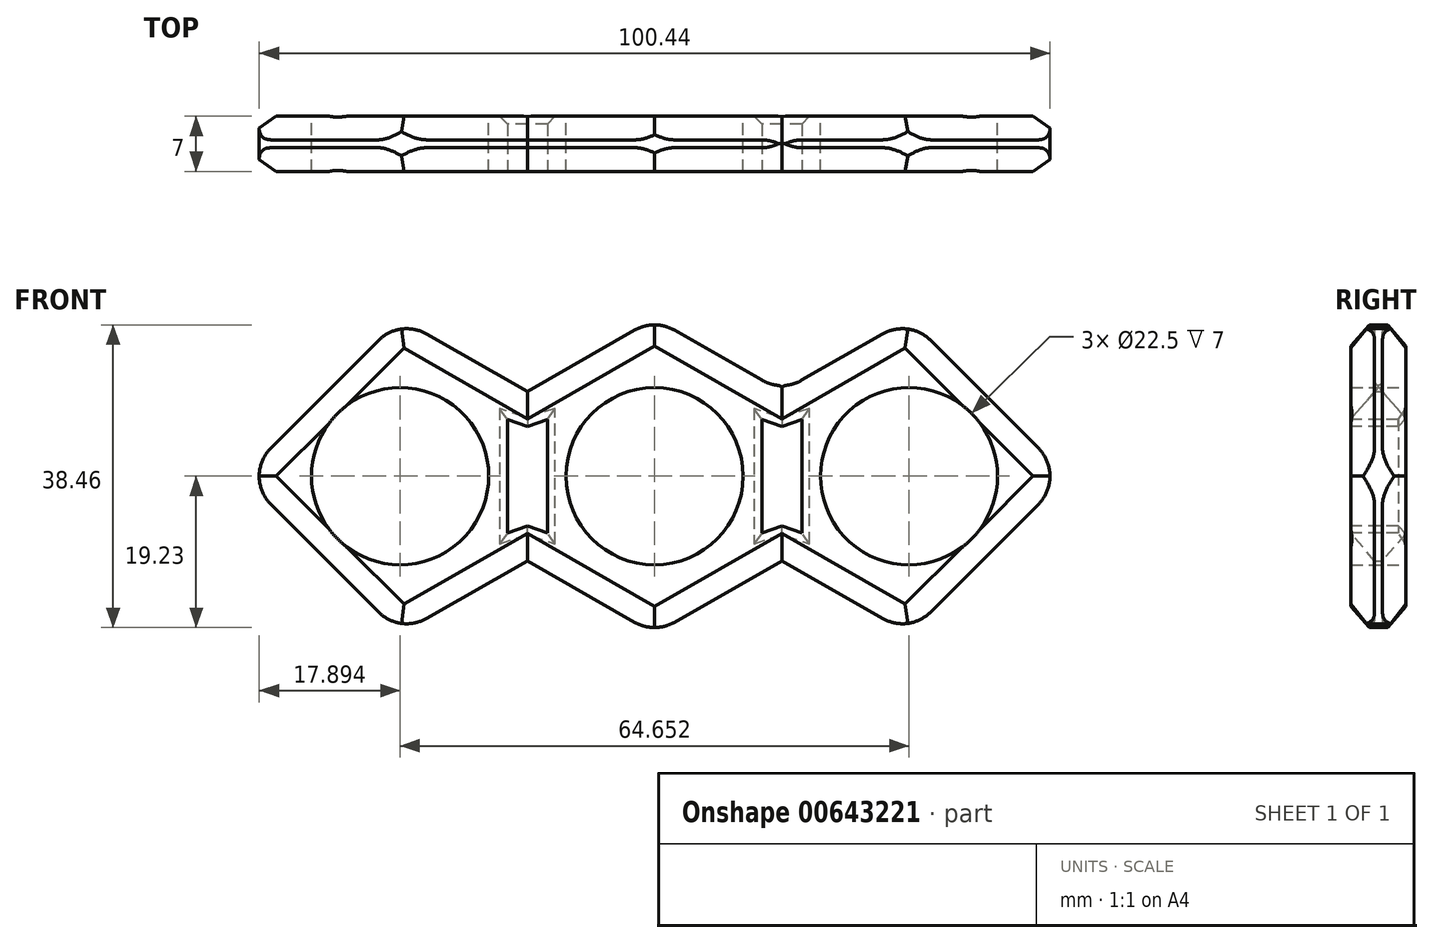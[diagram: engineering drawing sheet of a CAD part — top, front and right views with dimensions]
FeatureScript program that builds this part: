
annotation { "Feature Type Name" : "Feature", "Feature Type Description" : "" }
export const myFeature = defineFeature(function(context is Context, id is Id, definition is map)
    precondition{}
    {
        {
            var Q0;
            Q0=qCreatedBy(makeId("Front.planeOp"),FACE);
            var sketch = newSketch(context, id + "F0", { "sketchPlane" : qUnion([Q0])});
            skCircle(sketch, "E0", {"center": v(0, 0) * mm, "radius": 11.25 * mm});
            skLineSegment(sketch, "E1", {"start": v(0, 0) * mm, "end": v(-32.33, 0) * mm});
            skLineSegment(sketch, "E2.MirrorCS", {"start": v(0, 0) * mm, "end": v(32.33, 0) * mm});
            skCircle(sketch, "E3", {"center": v(-32.33, 0) * mm, "radius": 11.25 * mm});
            skCircle(sketch, "E4", {"center": v(32.33, 0) * mm, "radius": 11.25 * mm});
            skLineSegment(sketch, "E5", {"start": v(-32.33, 0) * mm, "end": v(-52.33, 0) * mm});
            skLineSegment(sketch, "E6.MirrorCS", {"start": v(32.33, 0) * mm, "end": v(52.33, 0) * mm});
            skLineSegment(sketch, "E7", {"start": v(-32.33, 0) * mm, "end": v(-32.33, 20) * mm});
            skLineSegment(sketch, "E8", {"start": v(-32.33, 0) * mm, "end": v(-32.33, -20) * mm});
            skLineSegment(sketch, "E9", {"start": v(-52.33, 0) * mm, "end": v(-32.33, -20) * mm});
            skLineSegment(sketch, "E10", {"start": v(-52.33, 0) * mm, "end": v(-32.33, 20) * mm});
            skLineSegment(sketch, "E11", {"start": v(-16.16, 0) * mm, "end": v(-16.16, 10.75) * mm});
            skLineSegment(sketch, "E12", {"start": v(-16.16, 10.75) * mm, "end": v(-32.33, 20) * mm});
            skLineSegment(sketch, "E13.MirrorCS", {"start": v(-16.16, -10.75) * mm, "end": v(-32.33, -20) * mm});
            skLineSegment(sketch, "E14.MirrorCS", {"start": v(-16.16, 0) * mm, "end": v(-16.16, -10.75) * mm});
            skLineSegment(sketch, "E15", {"start": v(0, 0) * mm, "end": v(0, 20) * mm});
            skLineSegment(sketch, "E16", {"start": v(0, 0) * mm, "end": v(0, -20) * mm});
            skLineSegment(sketch, "E17", {"start": v(-16.16, 10.75) * mm, "end": v(0, 20) * mm});
            skLineSegment(sketch, "E18", {"start": v(-16.16, -10.75) * mm, "end": v(0, -20) * mm});
            skLineSegment(sketch, "E19.MirrorCS", {"start": v(16.16, 10.75) * mm, "end": v(0, 20) * mm});
            skLineSegment(sketch, "E20.MirrorCS", {"start": v(16.16, -10.75) * mm, "end": v(0, -20) * mm});
            skLineSegment(sketch, "E21.MirrorCS", {"start": v(52.33, 0) * mm, "end": v(32.33, -20) * mm});
            skLineSegment(sketch, "E22.MirrorCS", {"start": v(52.33, 0) * mm, "end": v(32.33, 20) * mm});
            skLineSegment(sketch, "E23.MirrorCS", {"start": v(16.16, 10.75) * mm, "end": v(32.33, 20) * mm});
            skLineSegment(sketch, "E24.MirrorCS", {"start": v(16.16, -10.75) * mm, "end": v(32.33, -20) * mm});
            skLineSegment(sketch, "E25.MirrorCS", {"start": v(16.16, 0) * mm, "end": v(16.16, 10.75) * mm});
            skLineSegment(sketch, "E26.MirrorCS", {"start": v(16.16, 0) * mm, "end": v(16.16, -10.75) * mm});
            skSolve(sketch);
        }
        {
            var Q0;
            {var subQ0=sQuery(id+"F0.wireOp",EDGE,"E22.MirrorCS");Q0=makeQuery(id+"F0.imprint","IMPRINT",FACE,{"disambiguationData":[TD([[makeQuery(id+"F0.imprint","IMPRINT",EDGE,{"derivedFrom":subQ0}),1.0]])]});}
            var Q1;
            {var subQ0=sQuery(id+"F0.wireOp",EDGE,"E21.MirrorCS");Q1=makeQuery(id+"F0.imprint","IMPRINT",FACE,{"disambiguationData":[TD([[makeQuery(id+"F0.imprint","IMPRINT",EDGE,{"derivedFrom":subQ0}),-1.0]])]});}
            var Q2;
            {var subQ0=sQuery(id+"F0.wireOp",EDGE,"E20.MirrorCS");Q2=makeQuery(id+"F0.imprint","IMPRINT",FACE,{"disambiguationData":[TD([[makeQuery(id+"F0.imprint","IMPRINT",EDGE,{"derivedFrom":subQ0}),-1.0]])]});}
            var Q3;
            {var subQ0=sQuery(id+"F0.wireOp",EDGE,"E19.MirrorCS");Q3=makeQuery(id+"F0.imprint","IMPRINT",FACE,{"disambiguationData":[TD([[makeQuery(id+"F0.imprint","IMPRINT",EDGE,{"derivedFrom":subQ0}),1.0]])]});}
            var Q4;
            {var subQ4=sQuery(id+"F0.wireOp",EDGE,"E11");Q4=makeQuery(id+"F0.imprint","IMPRINT",FACE,{"disambiguationData":[TD([[makeQuery(id+"F0.imprint","IMPRINT",EDGE,{"derivedFrom":subQ4}),-1.0]])]});}
            var Q5;
            {var subQ0=sQuery(id+"F0.wireOp",EDGE,"E14.MirrorCS");Q5=makeQuery(id+"F0.imprint","IMPRINT",FACE,{"disambiguationData":[TD([[makeQuery(id+"F0.imprint","IMPRINT",EDGE,{"derivedFrom":subQ0}),1.0]])]});}
            var Q6;
            {var subQ0=sQuery(id+"F0.wireOp",EDGE,"E13.MirrorCS");Q6=makeQuery(id+"F0.imprint","IMPRINT",FACE,{"disambiguationData":[TD([[makeQuery(id+"F0.imprint","IMPRINT",EDGE,{"derivedFrom":subQ0}),-1.0]])]});}
            var Q7;
            {var subQ5=sQuery(id+"F0.wireOp",EDGE,"E9");Q7=makeQuery(id+"F0.imprint","IMPRINT",FACE,{"disambiguationData":[TD([[makeQuery(id+"F0.imprint","IMPRINT",EDGE,{"derivedFrom":subQ5}),1.0]])]});}
            var Q8;
            {var subQ5=sQuery(id+"F0.wireOp",EDGE,"E10");Q8=makeQuery(id+"F0.imprint","IMPRINT",FACE,{"disambiguationData":[TD([[makeQuery(id+"F0.imprint","IMPRINT",EDGE,{"derivedFrom":subQ5}),-1.0]])]});}
            var Q9;
            {var subQ0=sQuery(id+"F0.wireOp",EDGE,"E11");Q9=makeQuery(id+"F0.imprint","IMPRINT",FACE,{"disambiguationData":[TD([[makeQuery(id+"F0.imprint","IMPRINT",EDGE,{"derivedFrom":subQ0}),1.0]])]});}
            extrude(context, id + "F1", {"entities" : qUnion([Q0, Q1, Q2, Q3, Q4, Q5, Q6, Q7, Q8, Q9]), "depth" : 7 * mm, "offsetDistance" : 25.4 * mm});
        }
        {
            var Q0;
            Q0=makeQuery(id+"F1.opExtrude","CAP_FACE",FACE,{"disambiguationData":[OSD([sQuery(id+"F0.wireOp",EDGE,"E0"),sQuery(id+"F0.wireOp",EDGE,"E3"),sQuery(id+"F0.wireOp",EDGE,"E4"),sQuery(id+"F0.wireOp",EDGE,"E9"),sQuery(id+"F0.wireOp",EDGE,"E10"),sQuery(id+"F0.wireOp",EDGE,"E12"),sQuery(id+"F0.wireOp",EDGE,"E13.MirrorCS"),sQuery(id+"F0.wireOp",EDGE,"E17"),sQuery(id+"F0.wireOp",EDGE,"E18"),sQuery(id+"F0.wireOp",EDGE,"E19.MirrorCS"),sQuery(id+"F0.wireOp",EDGE,"E20.MirrorCS"),sQuery(id+"F0.wireOp",EDGE,"E21.MirrorCS"),sQuery(id+"F0.wireOp",EDGE,"E22.MirrorCS"),sQuery(id+"F0.wireOp",EDGE,"E23.MirrorCS"),sQuery(id+"F0.wireOp",EDGE,"E24.MirrorCS")])],"isStart":false});
            var sketch = newSketch(context, id + "F2", { "sketchPlane" : qUnion([Q0])});
            skLineSegment(sketch, "E27", {"start": v(16.16, -8.44) * mm, "end": v(16.16, 8.44) * mm});
            skLineSegment(sketch, "E28", {"start": v(-16.16, -8.44) * mm, "end": v(-16.16, 8.44) * mm});
            skLineSegment(sketch, "E29", {"start": v(13.63, -9.9) * mm, "end": v(13.63, 9.9) * mm});
            skLineSegment(sketch, "E30", {"start": v(13.63, 9.9) * mm, "end": v(18.7, 9.9) * mm});
            skLineSegment(sketch, "E31", {"start": v(18.7, 9.9) * mm, "end": v(18.7, -9.9) * mm});
            skLineSegment(sketch, "E32", {"start": v(13.63, -9.9) * mm, "end": v(16.16, -8.44) * mm});
            skLineSegment(sketch, "E33", {"start": v(16.16, -8.44) * mm, "end": v(18.7, -9.9) * mm});
            skLineSegment(sketch, "E34", {"start": v(13.63, 9.9) * mm, "end": v(16.16, 8.44) * mm});
            skLineSegment(sketch, "E35", {"start": v(16.16, 8.44) * mm, "end": v(18.7, 9.9) * mm});
            skLineSegment(sketch, "E36.MirrorCS", {"start": v(-13.63, -9.9) * mm, "end": v(-13.63, 9.9) * mm});
            skLineSegment(sketch, "E37.MirrorCS", {"start": v(-18.7, 9.9) * mm, "end": v(-18.7, -9.9) * mm});
            skLineSegment(sketch, "E38.MirrorCS", {"start": v(-16.16, 8.44) * mm, "end": v(-18.7, 9.9) * mm});
            skLineSegment(sketch, "E39.MirrorCS", {"start": v(-13.63, 9.9) * mm, "end": v(-16.16, 8.44) * mm});
            skLineSegment(sketch, "E40.MirrorCS", {"start": v(-16.16, -8.44) * mm, "end": v(-18.7, -9.9) * mm});
            skLineSegment(sketch, "E41.MirrorCS", {"start": v(-13.63, -9.9) * mm, "end": v(-16.16, -8.44) * mm});
            skLineSegment(sketch, "E42", {"start": v(-18.7, 7.21) * mm, "end": v(-16.16, 6.34) * mm});
            skLineSegment(sketch, "E43", {"start": v(-16.16, 6.34) * mm, "end": v(-13.63, 7.21) * mm});
            skLineSegment(sketch, "E44.MirrorCS", {"start": v(-16.16, -6.34) * mm, "end": v(-13.63, -7.21) * mm});
            skLineSegment(sketch, "E45.MirrorCS", {"start": v(-18.7, -7.21) * mm, "end": v(-16.16, -6.34) * mm});
            skLineSegment(sketch, "E46.MirrorCS", {"start": v(16.16, 6.34) * mm, "end": v(13.63, 7.21) * mm});
            skLineSegment(sketch, "E47.MirrorCS", {"start": v(18.7, 7.21) * mm, "end": v(16.16, 6.34) * mm});
            skLineSegment(sketch, "E48.MirrorCS", {"start": v(16.16, -6.34) * mm, "end": v(13.63, -7.21) * mm});
            skLineSegment(sketch, "E49.MirrorCS", {"start": v(18.7, -7.21) * mm, "end": v(16.16, -6.34) * mm});
            skSolve(sketch);
        }
        {
            var Q0;
            {var subQ0=sQuery(id+"F2.wireOp",EDGE,"E43");Q0=makeQuery(id+"F2.imprint","IMPRINT",FACE,{"disambiguationData":[TD([[makeQuery(id+"F2.imprint","IMPRINT",EDGE,{"derivedFrom":subQ0}),-1.0]])]});}
            var Q1;
            {var subQ0=sQuery(id+"F2.wireOp",EDGE,"E42");Q1=makeQuery(id+"F2.imprint","IMPRINT",FACE,{"disambiguationData":[TD([[makeQuery(id+"F2.imprint","IMPRINT",EDGE,{"derivedFrom":subQ0}),-1.0]])]});}
            var Q2;
            {var subQ0=sQuery(id+"F2.wireOp",EDGE,"E46.MirrorCS");Q2=makeQuery(id+"F2.imprint","IMPRINT",FACE,{"disambiguationData":[TD([[makeQuery(id+"F2.imprint","IMPRINT",EDGE,{"derivedFrom":subQ0}),1.0]])]});}
            var Q3;
            {var subQ0=sQuery(id+"F2.wireOp",EDGE,"E47.MirrorCS");Q3=makeQuery(id+"F2.imprint","IMPRINT",FACE,{"disambiguationData":[TD([[makeQuery(id+"F2.imprint","IMPRINT",EDGE,{"derivedFrom":subQ0}),1.0]])]});}
            extrude(context, id + "F3", {"entities" : qUnion([Q0, Q1, Q2, Q3]), "operationType" : NewBodyOperationType.REMOVE, "oppositeDirection" : true, "depth" : 127 * mm, "offsetDistance" : 25.4 * mm});
        }
        {
            var Q0;
            Q0=makeQuery(id+"F1.opExtrude","CAP_EDGE",EDGE,{"disambiguationData":[OSD([sQuery(id+"F0.wireOp",EDGE,"E12")])],"isStart":false});
            var Q1;
            Q1=makeQuery(id+"F1.opExtrude","CAP_EDGE",EDGE,{"disambiguationData":[OSD([sQuery(id+"F0.wireOp",EDGE,"E17")])],"isStart":false});
            var Q2;
            Q2=makeQuery(id+"F1.opExtrude","CAP_EDGE",EDGE,{"disambiguationData":[OSD([sQuery(id+"F0.wireOp",EDGE,"E19.MirrorCS")])],"isStart":false});
            var Q3;
            Q3=makeQuery(id+"F1.opExtrude","CAP_EDGE",EDGE,{"disambiguationData":[OSD([sQuery(id+"F0.wireOp",EDGE,"E23.MirrorCS")])],"isStart":false});
            var Q4;
            Q4=makeQuery(id+"F1.opExtrude","CAP_EDGE",EDGE,{"disambiguationData":[OSD([sQuery(id+"F0.wireOp",EDGE,"E22.MirrorCS")])],"isStart":false});
            var Q5;
            Q5=makeQuery(id+"F1.opExtrude","CAP_EDGE",EDGE,{"disambiguationData":[OSD([sQuery(id+"F0.wireOp",EDGE,"E22.MirrorCS")])],"isStart":true});
            var Q6;
            Q6=makeQuery(id+"F1.opExtrude","CAP_EDGE",EDGE,{"disambiguationData":[OSD([sQuery(id+"F0.wireOp",EDGE,"E23.MirrorCS")])],"isStart":true});
            var Q7;
            Q7=makeQuery(id+"F1.opExtrude","CAP_EDGE",EDGE,{"disambiguationData":[OSD([sQuery(id+"F0.wireOp",EDGE,"E19.MirrorCS")])],"isStart":true});
            var Q8;
            Q8=makeQuery(id+"F1.opExtrude","CAP_EDGE",EDGE,{"disambiguationData":[OSD([sQuery(id+"F0.wireOp",EDGE,"E17")])],"isStart":true});
            var Q9;
            Q9=makeQuery(id+"F1.opExtrude","CAP_EDGE",EDGE,{"disambiguationData":[OSD([sQuery(id+"F0.wireOp",EDGE,"E12")])],"isStart":true});
            var Q10;
            Q10=makeQuery(id+"F1.opExtrude","CAP_EDGE",EDGE,{"disambiguationData":[OSD([sQuery(id+"F0.wireOp",EDGE,"E10")])],"isStart":false});
            var Q11;
            Q11=makeQuery(id+"F1.opExtrude","CAP_EDGE",EDGE,{"disambiguationData":[OSD([sQuery(id+"F0.wireOp",EDGE,"E10")])],"isStart":true});
            var Q12;
            Q12=makeQuery(id+"F1.opExtrude","CAP_EDGE",EDGE,{"disambiguationData":[OSD([sQuery(id+"F0.wireOp",EDGE,"E9")])],"isStart":false});
            var Q13;
            Q13=makeQuery(id+"F1.opExtrude","CAP_EDGE",EDGE,{"disambiguationData":[OSD([sQuery(id+"F0.wireOp",EDGE,"E9")])],"isStart":true});
            var Q14;
            Q14=makeQuery(id+"F1.opExtrude","CAP_EDGE",EDGE,{"disambiguationData":[OSD([sQuery(id+"F0.wireOp",EDGE,"E13.MirrorCS")])],"isStart":true});
            var Q15;
            Q15=makeQuery(id+"F1.opExtrude","CAP_EDGE",EDGE,{"disambiguationData":[OSD([sQuery(id+"F0.wireOp",EDGE,"E13.MirrorCS")])],"isStart":false});
            var Q16;
            Q16=makeQuery(id+"F1.opExtrude","CAP_EDGE",EDGE,{"disambiguationData":[OSD([sQuery(id+"F0.wireOp",EDGE,"E18")])],"isStart":false});
            var Q17;
            Q17=makeQuery(id+"F1.opExtrude","CAP_EDGE",EDGE,{"disambiguationData":[OSD([sQuery(id+"F0.wireOp",EDGE,"E18")])],"isStart":true});
            var Q18;
            Q18=makeQuery(id+"F1.opExtrude","CAP_EDGE",EDGE,{"disambiguationData":[OSD([sQuery(id+"F0.wireOp",EDGE,"E20.MirrorCS")])],"isStart":true});
            var Q19;
            Q19=makeQuery(id+"F1.opExtrude","CAP_EDGE",EDGE,{"disambiguationData":[OSD([sQuery(id+"F0.wireOp",EDGE,"E20.MirrorCS")])],"isStart":false});
            var Q20;
            Q20=makeQuery(id+"F1.opExtrude","CAP_EDGE",EDGE,{"disambiguationData":[OSD([sQuery(id+"F0.wireOp",EDGE,"E24.MirrorCS")])],"isStart":true});
            var Q21;
            Q21=makeQuery(id+"F1.opExtrude","CAP_EDGE",EDGE,{"disambiguationData":[OSD([sQuery(id+"F0.wireOp",EDGE,"E24.MirrorCS")])],"isStart":false});
            var Q22;
            Q22=makeQuery(id+"F1.opExtrude","CAP_EDGE",EDGE,{"disambiguationData":[OSD([sQuery(id+"F0.wireOp",EDGE,"E21.MirrorCS")])],"isStart":true});
            var Q23;
            Q23=makeQuery(id+"F1.opExtrude","CAP_EDGE",EDGE,{"disambiguationData":[OSD([sQuery(id+"F0.wireOp",EDGE,"E21.MirrorCS")])],"isStart":false});
            chamfer(context, id + "F4", {"entities" : qUnion([Q0, Q1, Q2, Q3, Q4, Q5, Q6, Q7, Q8, Q9, Q10, Q11, Q12, Q13, Q14, Q15, Q16, Q17, Q18, Q19, Q20, Q21, Q22, Q23]), "width" : 3 * mm, "tangentPropagation" : true});
        }
        {
            var Q0;
            Q0=makeQuery(id+"F1.opExtrude","SWEPT_EDGE",EDGE,{"disambiguationData":[OSD([sQuery(id+"F0.wireOp",EDGE,"E5"),sQuery(id+"F0.wireOp",EDGE,"E9"),sQuery(id+"F0.wireOp",EDGE,"E10")])]});
            var Q1;
            Q1=makeQuery(id+"F1.opExtrude","SWEPT_EDGE",EDGE,{"disambiguationData":[OSD([sQuery(id+"F0.wireOp",EDGE,"E8"),sQuery(id+"F0.wireOp",EDGE,"E9"),sQuery(id+"F0.wireOp",EDGE,"E13.MirrorCS")])]});
            var Q2;
            Q2=makeQuery(id+"F1.opExtrude","SWEPT_EDGE",EDGE,{"disambiguationData":[OSD([sQuery(id+"F0.wireOp",EDGE,"E16"),sQuery(id+"F0.wireOp",EDGE,"E18"),sQuery(id+"F0.wireOp",EDGE,"E20.MirrorCS")])]});
            var Q3;
            Q3=makeQuery(id+"F1.opExtrude","SWEPT_EDGE",EDGE,{"disambiguationData":[OSD([sQuery(id+"F0.wireOp",EDGE,"E21.MirrorCS"),sQuery(id+"F0.wireOp",EDGE,"E24.MirrorCS")])]});
            var Q4;
            Q4=makeQuery(id+"F1.opExtrude","SWEPT_EDGE",EDGE,{"disambiguationData":[OSD([sQuery(id+"F0.wireOp",EDGE,"E6.MirrorCS"),sQuery(id+"F0.wireOp",EDGE,"E21.MirrorCS"),sQuery(id+"F0.wireOp",EDGE,"E22.MirrorCS")])]});
            var Q5;
            Q5=makeQuery(id+"F1.opExtrude","SWEPT_EDGE",EDGE,{"disambiguationData":[OSD([sQuery(id+"F0.wireOp",EDGE,"E22.MirrorCS"),sQuery(id+"F0.wireOp",EDGE,"E23.MirrorCS")])]});
            var Q6;
            Q6=makeQuery(id+"F1.opExtrude","SWEPT_EDGE",EDGE,{"disambiguationData":[OSD([sQuery(id+"F0.wireOp",EDGE,"E19.MirrorCS"),sQuery(id+"F0.wireOp",EDGE,"E23.MirrorCS"),sQuery(id+"F0.wireOp",EDGE,"E25.MirrorCS")])]});
            var Q7;
            Q7=makeQuery(id+"F1.opExtrude","SWEPT_EDGE",EDGE,{"disambiguationData":[OSD([sQuery(id+"F0.wireOp",EDGE,"E15"),sQuery(id+"F0.wireOp",EDGE,"E17"),sQuery(id+"F0.wireOp",EDGE,"E19.MirrorCS")])]});
            var Q8;
            Q8=makeQuery(id+"F1.opExtrude","SWEPT_EDGE",EDGE,{"disambiguationData":[OSD([sQuery(id+"F0.wireOp",EDGE,"E7"),sQuery(id+"F0.wireOp",EDGE,"E10"),sQuery(id+"F0.wireOp",EDGE,"E12")])]});
            fillet(context, id + "F5", {"entities" : qUnion([Q0, Q1, Q2, Q3, Q4, Q5, Q6, Q7, Q8]), "radius" : 5.08 * mm, "tangentPropagation" : true, "allowEdgeOverflow" : false});
        }
        {
            var Q0;
            Q0=makeQuery(id+"F3.boolean.opBoolean","INTERSECT",EDGE,{"derivedFrom":[makeQuery(id+"F1.opExtrude","CAP_FACE",FACE,{"disambiguationData":[OSD([sQuery(id+"F0.wireOp",EDGE,"E0"),sQuery(id+"F0.wireOp",EDGE,"E3"),sQuery(id+"F0.wireOp",EDGE,"E4"),sQuery(id+"F0.wireOp",EDGE,"E9"),sQuery(id+"F0.wireOp",EDGE,"E10"),sQuery(id+"F0.wireOp",EDGE,"E12"),sQuery(id+"F0.wireOp",EDGE,"E13.MirrorCS"),sQuery(id+"F0.wireOp",EDGE,"E17"),sQuery(id+"F0.wireOp",EDGE,"E18"),sQuery(id+"F0.wireOp",EDGE,"E19.MirrorCS"),sQuery(id+"F0.wireOp",EDGE,"E20.MirrorCS"),sQuery(id+"F0.wireOp",EDGE,"E21.MirrorCS"),sQuery(id+"F0.wireOp",EDGE,"E22.MirrorCS"),sQuery(id+"F0.wireOp",EDGE,"E23.MirrorCS"),sQuery(id+"F0.wireOp",EDGE,"E24.MirrorCS")])],"isStart":true}),makeQuery(id+"F3.opExtrude","SWEPT_FACE",FACE,{"disambiguationData":[OSD([sQuery(id+"F2.wireOp",EDGE,"E36.MirrorCS")])]})]});
            var Q1;
            Q1=makeQuery(id+"F3.boolean.opBoolean","INTERSECT",EDGE,{"derivedFrom":[makeQuery(id+"F1.opExtrude","CAP_FACE",FACE,{"disambiguationData":[OSD([sQuery(id+"F0.wireOp",EDGE,"E0"),sQuery(id+"F0.wireOp",EDGE,"E3"),sQuery(id+"F0.wireOp",EDGE,"E4"),sQuery(id+"F0.wireOp",EDGE,"E9"),sQuery(id+"F0.wireOp",EDGE,"E10"),sQuery(id+"F0.wireOp",EDGE,"E12"),sQuery(id+"F0.wireOp",EDGE,"E13.MirrorCS"),sQuery(id+"F0.wireOp",EDGE,"E17"),sQuery(id+"F0.wireOp",EDGE,"E18"),sQuery(id+"F0.wireOp",EDGE,"E19.MirrorCS"),sQuery(id+"F0.wireOp",EDGE,"E20.MirrorCS"),sQuery(id+"F0.wireOp",EDGE,"E21.MirrorCS"),sQuery(id+"F0.wireOp",EDGE,"E22.MirrorCS"),sQuery(id+"F0.wireOp",EDGE,"E23.MirrorCS"),sQuery(id+"F0.wireOp",EDGE,"E24.MirrorCS")])],"isStart":true}),makeQuery(id+"F3.opExtrude","SWEPT_FACE",FACE,{"disambiguationData":[OSD([sQuery(id+"F2.wireOp",EDGE,"E37.MirrorCS")])]})]});
            var Q2;
            Q2=makeQuery(id+"F3.boolean.opBoolean","COPY",EDGE,{"derivedFrom":makeQuery(id+"F3.opExtrude","CAP_EDGE",EDGE,{"disambiguationData":[OSD([sQuery(id+"F2.wireOp",EDGE,"E37.MirrorCS")])],"isStart":true})});
            var Q3;
            Q3=makeQuery(id+"F3.boolean.opBoolean","COPY",EDGE,{"derivedFrom":makeQuery(id+"F3.opExtrude","CAP_EDGE",EDGE,{"disambiguationData":[OSD([sQuery(id+"F2.wireOp",EDGE,"E36.MirrorCS")])],"isStart":true})});
            var Q4;
            Q4=makeQuery(id+"F3.boolean.opBoolean","COPY",EDGE,{"derivedFrom":makeQuery(id+"F3.opExtrude","CAP_EDGE",EDGE,{"disambiguationData":[OSD([sQuery(id+"F2.wireOp",EDGE,"E29")])],"isStart":true})});
            var Q5;
            Q5=makeQuery(id+"F3.boolean.opBoolean","COPY",EDGE,{"derivedFrom":makeQuery(id+"F3.opExtrude","CAP_EDGE",EDGE,{"disambiguationData":[OSD([sQuery(id+"F2.wireOp",EDGE,"E31")])],"isStart":true})});
            var Q6;
            Q6=makeQuery(id+"F3.boolean.opBoolean","INTERSECT",EDGE,{"derivedFrom":[makeQuery(id+"F1.opExtrude","CAP_FACE",FACE,{"disambiguationData":[OSD([sQuery(id+"F0.wireOp",EDGE,"E0"),sQuery(id+"F0.wireOp",EDGE,"E3"),sQuery(id+"F0.wireOp",EDGE,"E4"),sQuery(id+"F0.wireOp",EDGE,"E9"),sQuery(id+"F0.wireOp",EDGE,"E10"),sQuery(id+"F0.wireOp",EDGE,"E12"),sQuery(id+"F0.wireOp",EDGE,"E13.MirrorCS"),sQuery(id+"F0.wireOp",EDGE,"E17"),sQuery(id+"F0.wireOp",EDGE,"E18"),sQuery(id+"F0.wireOp",EDGE,"E19.MirrorCS"),sQuery(id+"F0.wireOp",EDGE,"E20.MirrorCS"),sQuery(id+"F0.wireOp",EDGE,"E21.MirrorCS"),sQuery(id+"F0.wireOp",EDGE,"E22.MirrorCS"),sQuery(id+"F0.wireOp",EDGE,"E23.MirrorCS"),sQuery(id+"F0.wireOp",EDGE,"E24.MirrorCS")])],"isStart":true}),makeQuery(id+"F3.opExtrude","SWEPT_FACE",FACE,{"disambiguationData":[OSD([sQuery(id+"F2.wireOp",EDGE,"E31")])]})]});
            var Q7;
            Q7=makeQuery(id+"F3.boolean.opBoolean","INTERSECT",EDGE,{"derivedFrom":[makeQuery(id+"F1.opExtrude","CAP_FACE",FACE,{"disambiguationData":[OSD([sQuery(id+"F0.wireOp",EDGE,"E0"),sQuery(id+"F0.wireOp",EDGE,"E3"),sQuery(id+"F0.wireOp",EDGE,"E4"),sQuery(id+"F0.wireOp",EDGE,"E9"),sQuery(id+"F0.wireOp",EDGE,"E10"),sQuery(id+"F0.wireOp",EDGE,"E12"),sQuery(id+"F0.wireOp",EDGE,"E13.MirrorCS"),sQuery(id+"F0.wireOp",EDGE,"E17"),sQuery(id+"F0.wireOp",EDGE,"E18"),sQuery(id+"F0.wireOp",EDGE,"E19.MirrorCS"),sQuery(id+"F0.wireOp",EDGE,"E20.MirrorCS"),sQuery(id+"F0.wireOp",EDGE,"E21.MirrorCS"),sQuery(id+"F0.wireOp",EDGE,"E22.MirrorCS"),sQuery(id+"F0.wireOp",EDGE,"E23.MirrorCS"),sQuery(id+"F0.wireOp",EDGE,"E24.MirrorCS")])],"isStart":true}),makeQuery(id+"F3.opExtrude","SWEPT_FACE",FACE,{"disambiguationData":[OSD([sQuery(id+"F2.wireOp",EDGE,"E29")])]})]});
            var Q8;
            {var subQ0=sQuery(id+"F0.wireOp",EDGE,"E23.MirrorCS");Q8=makeQuery(id+"F5.opFillet","BLEND_EDGE",EDGE,{"blendedFrom":[makeQuery(id+"F1.opExtrude","SWEPT_EDGE",EDGE,{"disambiguationData":[OSD([sQuery(id+"F0.wireOp",EDGE,"E19.MirrorCS"),subQ0,sQuery(id+"F0.wireOp",EDGE,"E25.MirrorCS")])]}),makeQuery(id+"F1.opExtrude","SWEPT_FACE",FACE,{"disambiguationData":[OSD([subQ0])]})],"blendedInto":[makeQuery(id+"F1.opExtrude","SWEPT_FACE",FACE,{"disambiguationData":[OSD([subQ0])]})]});}
            var Q9;
            Q9=makeQuery(id+"F3.boolean.opBoolean","INTERSECT",EDGE,{"derivedFrom":[makeQuery(id+"F1.opExtrude","CAP_FACE",FACE,{"disambiguationData":[OSD([sQuery(id+"F0.wireOp",EDGE,"E0"),sQuery(id+"F0.wireOp",EDGE,"E3"),sQuery(id+"F0.wireOp",EDGE,"E4"),sQuery(id+"F0.wireOp",EDGE,"E9"),sQuery(id+"F0.wireOp",EDGE,"E10"),sQuery(id+"F0.wireOp",EDGE,"E12"),sQuery(id+"F0.wireOp",EDGE,"E13.MirrorCS"),sQuery(id+"F0.wireOp",EDGE,"E17"),sQuery(id+"F0.wireOp",EDGE,"E18"),sQuery(id+"F0.wireOp",EDGE,"E19.MirrorCS"),sQuery(id+"F0.wireOp",EDGE,"E20.MirrorCS"),sQuery(id+"F0.wireOp",EDGE,"E21.MirrorCS"),sQuery(id+"F0.wireOp",EDGE,"E22.MirrorCS"),sQuery(id+"F0.wireOp",EDGE,"E23.MirrorCS"),sQuery(id+"F0.wireOp",EDGE,"E24.MirrorCS")])],"isStart":true}),makeQuery(id+"F3.opExtrude","SWEPT_FACE",FACE,{"disambiguationData":[OSD([sQuery(id+"F2.wireOp",EDGE,"E49.MirrorCS")])]})]});
            var Q10;
            Q10=makeQuery(id+"F3.boolean.opBoolean","INTERSECT",EDGE,{"derivedFrom":[makeQuery(id+"F1.opExtrude","CAP_FACE",FACE,{"disambiguationData":[OSD([sQuery(id+"F0.wireOp",EDGE,"E0"),sQuery(id+"F0.wireOp",EDGE,"E3"),sQuery(id+"F0.wireOp",EDGE,"E4"),sQuery(id+"F0.wireOp",EDGE,"E9"),sQuery(id+"F0.wireOp",EDGE,"E10"),sQuery(id+"F0.wireOp",EDGE,"E12"),sQuery(id+"F0.wireOp",EDGE,"E13.MirrorCS"),sQuery(id+"F0.wireOp",EDGE,"E17"),sQuery(id+"F0.wireOp",EDGE,"E18"),sQuery(id+"F0.wireOp",EDGE,"E19.MirrorCS"),sQuery(id+"F0.wireOp",EDGE,"E20.MirrorCS"),sQuery(id+"F0.wireOp",EDGE,"E21.MirrorCS"),sQuery(id+"F0.wireOp",EDGE,"E22.MirrorCS"),sQuery(id+"F0.wireOp",EDGE,"E23.MirrorCS"),sQuery(id+"F0.wireOp",EDGE,"E24.MirrorCS")])],"isStart":true}),makeQuery(id+"F3.opExtrude","SWEPT_FACE",FACE,{"disambiguationData":[OSD([sQuery(id+"F2.wireOp",EDGE,"E48.MirrorCS")])]})]});
            var Q11;
            Q11=makeQuery(id+"F3.boolean.opBoolean","INTERSECT",EDGE,{"derivedFrom":[makeQuery(id+"F1.opExtrude","CAP_FACE",FACE,{"disambiguationData":[OSD([sQuery(id+"F0.wireOp",EDGE,"E0"),sQuery(id+"F0.wireOp",EDGE,"E3"),sQuery(id+"F0.wireOp",EDGE,"E4"),sQuery(id+"F0.wireOp",EDGE,"E9"),sQuery(id+"F0.wireOp",EDGE,"E10"),sQuery(id+"F0.wireOp",EDGE,"E12"),sQuery(id+"F0.wireOp",EDGE,"E13.MirrorCS"),sQuery(id+"F0.wireOp",EDGE,"E17"),sQuery(id+"F0.wireOp",EDGE,"E18"),sQuery(id+"F0.wireOp",EDGE,"E19.MirrorCS"),sQuery(id+"F0.wireOp",EDGE,"E20.MirrorCS"),sQuery(id+"F0.wireOp",EDGE,"E21.MirrorCS"),sQuery(id+"F0.wireOp",EDGE,"E22.MirrorCS"),sQuery(id+"F0.wireOp",EDGE,"E23.MirrorCS"),sQuery(id+"F0.wireOp",EDGE,"E24.MirrorCS")])],"isStart":true}),makeQuery(id+"F3.opExtrude","SWEPT_FACE",FACE,{"disambiguationData":[OSD([sQuery(id+"F2.wireOp",EDGE,"E47.MirrorCS")])]})]});
            var Q12;
            Q12=makeQuery(id+"F3.boolean.opBoolean","INTERSECT",EDGE,{"derivedFrom":[makeQuery(id+"F1.opExtrude","CAP_FACE",FACE,{"disambiguationData":[OSD([sQuery(id+"F0.wireOp",EDGE,"E0"),sQuery(id+"F0.wireOp",EDGE,"E3"),sQuery(id+"F0.wireOp",EDGE,"E4"),sQuery(id+"F0.wireOp",EDGE,"E9"),sQuery(id+"F0.wireOp",EDGE,"E10"),sQuery(id+"F0.wireOp",EDGE,"E12"),sQuery(id+"F0.wireOp",EDGE,"E13.MirrorCS"),sQuery(id+"F0.wireOp",EDGE,"E17"),sQuery(id+"F0.wireOp",EDGE,"E18"),sQuery(id+"F0.wireOp",EDGE,"E19.MirrorCS"),sQuery(id+"F0.wireOp",EDGE,"E20.MirrorCS"),sQuery(id+"F0.wireOp",EDGE,"E21.MirrorCS"),sQuery(id+"F0.wireOp",EDGE,"E22.MirrorCS"),sQuery(id+"F0.wireOp",EDGE,"E23.MirrorCS"),sQuery(id+"F0.wireOp",EDGE,"E24.MirrorCS")])],"isStart":true}),makeQuery(id+"F3.opExtrude","SWEPT_FACE",FACE,{"disambiguationData":[OSD([sQuery(id+"F2.wireOp",EDGE,"E46.MirrorCS")])]})]});
            var Q13;
            Q13=makeQuery(id+"F3.boolean.opBoolean","COPY",EDGE,{"derivedFrom":makeQuery(id+"F3.opExtrude","CAP_EDGE",EDGE,{"disambiguationData":[OSD([sQuery(id+"F2.wireOp",EDGE,"E46.MirrorCS")])],"isStart":true})});
            var Q14;
            Q14=makeQuery(id+"F3.boolean.opBoolean","COPY",EDGE,{"derivedFrom":makeQuery(id+"F3.opExtrude","CAP_EDGE",EDGE,{"disambiguationData":[OSD([sQuery(id+"F2.wireOp",EDGE,"E47.MirrorCS")])],"isStart":true})});
            var Q15;
            Q15=makeQuery(id+"F3.boolean.opBoolean","COPY",EDGE,{"derivedFrom":makeQuery(id+"F3.opExtrude","CAP_EDGE",EDGE,{"disambiguationData":[OSD([sQuery(id+"F2.wireOp",EDGE,"E48.MirrorCS")])],"isStart":true})});
            var Q16;
            Q16=makeQuery(id+"F3.boolean.opBoolean","COPY",EDGE,{"derivedFrom":makeQuery(id+"F3.opExtrude","CAP_EDGE",EDGE,{"disambiguationData":[OSD([sQuery(id+"F2.wireOp",EDGE,"E49.MirrorCS")])],"isStart":true})});
            var Q17;
            Q17=makeQuery(id+"F3.boolean.opBoolean","COPY",EDGE,{"derivedFrom":makeQuery(id+"F3.opExtrude","CAP_EDGE",EDGE,{"disambiguationData":[OSD([sQuery(id+"F2.wireOp",EDGE,"E45.MirrorCS")])],"isStart":true})});
            var Q18;
            Q18=makeQuery(id+"F3.boolean.opBoolean","COPY",EDGE,{"derivedFrom":makeQuery(id+"F3.opExtrude","CAP_EDGE",EDGE,{"disambiguationData":[OSD([sQuery(id+"F2.wireOp",EDGE,"E44.MirrorCS")])],"isStart":true})});
            var Q19;
            Q19=makeQuery(id+"F3.boolean.opBoolean","COPY",EDGE,{"derivedFrom":makeQuery(id+"F3.opExtrude","CAP_EDGE",EDGE,{"disambiguationData":[OSD([sQuery(id+"F2.wireOp",EDGE,"E43")])],"isStart":true})});
            var Q20;
            Q20=makeQuery(id+"F3.boolean.opBoolean","COPY",EDGE,{"derivedFrom":makeQuery(id+"F3.opExtrude","CAP_EDGE",EDGE,{"disambiguationData":[OSD([sQuery(id+"F2.wireOp",EDGE,"E42")])],"isStart":true})});
            var Q21;
            Q21=makeQuery(id+"F3.boolean.opBoolean","INTERSECT",EDGE,{"derivedFrom":[makeQuery(id+"F1.opExtrude","CAP_FACE",FACE,{"disambiguationData":[OSD([sQuery(id+"F0.wireOp",EDGE,"E0"),sQuery(id+"F0.wireOp",EDGE,"E3"),sQuery(id+"F0.wireOp",EDGE,"E4"),sQuery(id+"F0.wireOp",EDGE,"E9"),sQuery(id+"F0.wireOp",EDGE,"E10"),sQuery(id+"F0.wireOp",EDGE,"E12"),sQuery(id+"F0.wireOp",EDGE,"E13.MirrorCS"),sQuery(id+"F0.wireOp",EDGE,"E17"),sQuery(id+"F0.wireOp",EDGE,"E18"),sQuery(id+"F0.wireOp",EDGE,"E19.MirrorCS"),sQuery(id+"F0.wireOp",EDGE,"E20.MirrorCS"),sQuery(id+"F0.wireOp",EDGE,"E21.MirrorCS"),sQuery(id+"F0.wireOp",EDGE,"E22.MirrorCS"),sQuery(id+"F0.wireOp",EDGE,"E23.MirrorCS"),sQuery(id+"F0.wireOp",EDGE,"E24.MirrorCS")])],"isStart":true}),makeQuery(id+"F3.opExtrude","SWEPT_FACE",FACE,{"disambiguationData":[OSD([sQuery(id+"F2.wireOp",EDGE,"E44.MirrorCS")])]})]});
            var Q22;
            Q22=makeQuery(id+"F3.boolean.opBoolean","INTERSECT",EDGE,{"derivedFrom":[makeQuery(id+"F1.opExtrude","CAP_FACE",FACE,{"disambiguationData":[OSD([sQuery(id+"F0.wireOp",EDGE,"E0"),sQuery(id+"F0.wireOp",EDGE,"E3"),sQuery(id+"F0.wireOp",EDGE,"E4"),sQuery(id+"F0.wireOp",EDGE,"E9"),sQuery(id+"F0.wireOp",EDGE,"E10"),sQuery(id+"F0.wireOp",EDGE,"E12"),sQuery(id+"F0.wireOp",EDGE,"E13.MirrorCS"),sQuery(id+"F0.wireOp",EDGE,"E17"),sQuery(id+"F0.wireOp",EDGE,"E18"),sQuery(id+"F0.wireOp",EDGE,"E19.MirrorCS"),sQuery(id+"F0.wireOp",EDGE,"E20.MirrorCS"),sQuery(id+"F0.wireOp",EDGE,"E21.MirrorCS"),sQuery(id+"F0.wireOp",EDGE,"E22.MirrorCS"),sQuery(id+"F0.wireOp",EDGE,"E23.MirrorCS"),sQuery(id+"F0.wireOp",EDGE,"E24.MirrorCS")])],"isStart":true}),makeQuery(id+"F3.opExtrude","SWEPT_FACE",FACE,{"disambiguationData":[OSD([sQuery(id+"F2.wireOp",EDGE,"E45.MirrorCS")])]})]});
            var Q23;
            Q23=makeQuery(id+"F3.boolean.opBoolean","INTERSECT",EDGE,{"derivedFrom":[makeQuery(id+"F1.opExtrude","CAP_FACE",FACE,{"disambiguationData":[OSD([sQuery(id+"F0.wireOp",EDGE,"E0"),sQuery(id+"F0.wireOp",EDGE,"E3"),sQuery(id+"F0.wireOp",EDGE,"E4"),sQuery(id+"F0.wireOp",EDGE,"E9"),sQuery(id+"F0.wireOp",EDGE,"E10"),sQuery(id+"F0.wireOp",EDGE,"E12"),sQuery(id+"F0.wireOp",EDGE,"E13.MirrorCS"),sQuery(id+"F0.wireOp",EDGE,"E17"),sQuery(id+"F0.wireOp",EDGE,"E18"),sQuery(id+"F0.wireOp",EDGE,"E19.MirrorCS"),sQuery(id+"F0.wireOp",EDGE,"E20.MirrorCS"),sQuery(id+"F0.wireOp",EDGE,"E21.MirrorCS"),sQuery(id+"F0.wireOp",EDGE,"E22.MirrorCS"),sQuery(id+"F0.wireOp",EDGE,"E23.MirrorCS"),sQuery(id+"F0.wireOp",EDGE,"E24.MirrorCS")])],"isStart":true}),makeQuery(id+"F3.opExtrude","SWEPT_FACE",FACE,{"disambiguationData":[OSD([sQuery(id+"F2.wireOp",EDGE,"E42")])]})]});
            var Q24;
            Q24=makeQuery(id+"F3.boolean.opBoolean","INTERSECT",EDGE,{"derivedFrom":[makeQuery(id+"F1.opExtrude","CAP_FACE",FACE,{"disambiguationData":[OSD([sQuery(id+"F0.wireOp",EDGE,"E0"),sQuery(id+"F0.wireOp",EDGE,"E3"),sQuery(id+"F0.wireOp",EDGE,"E4"),sQuery(id+"F0.wireOp",EDGE,"E9"),sQuery(id+"F0.wireOp",EDGE,"E10"),sQuery(id+"F0.wireOp",EDGE,"E12"),sQuery(id+"F0.wireOp",EDGE,"E13.MirrorCS"),sQuery(id+"F0.wireOp",EDGE,"E17"),sQuery(id+"F0.wireOp",EDGE,"E18"),sQuery(id+"F0.wireOp",EDGE,"E19.MirrorCS"),sQuery(id+"F0.wireOp",EDGE,"E20.MirrorCS"),sQuery(id+"F0.wireOp",EDGE,"E21.MirrorCS"),sQuery(id+"F0.wireOp",EDGE,"E22.MirrorCS"),sQuery(id+"F0.wireOp",EDGE,"E23.MirrorCS"),sQuery(id+"F0.wireOp",EDGE,"E24.MirrorCS")])],"isStart":true}),makeQuery(id+"F3.opExtrude","SWEPT_FACE",FACE,{"disambiguationData":[OSD([sQuery(id+"F2.wireOp",EDGE,"E43")])]})]});
            chamfer(context, id + "F6", {"entities" : qUnion([Q0, Q1, Q2, Q3, Q4, Q5, Q6, Q7, Q8, Q9, Q10, Q11, Q12, Q13, Q14, Q15, Q16, Q17, Q18, Q19, Q20, Q21, Q22, Q23, Q24]), "width" : 1 * mm, "tangentPropagation" : true});
        }
    });
